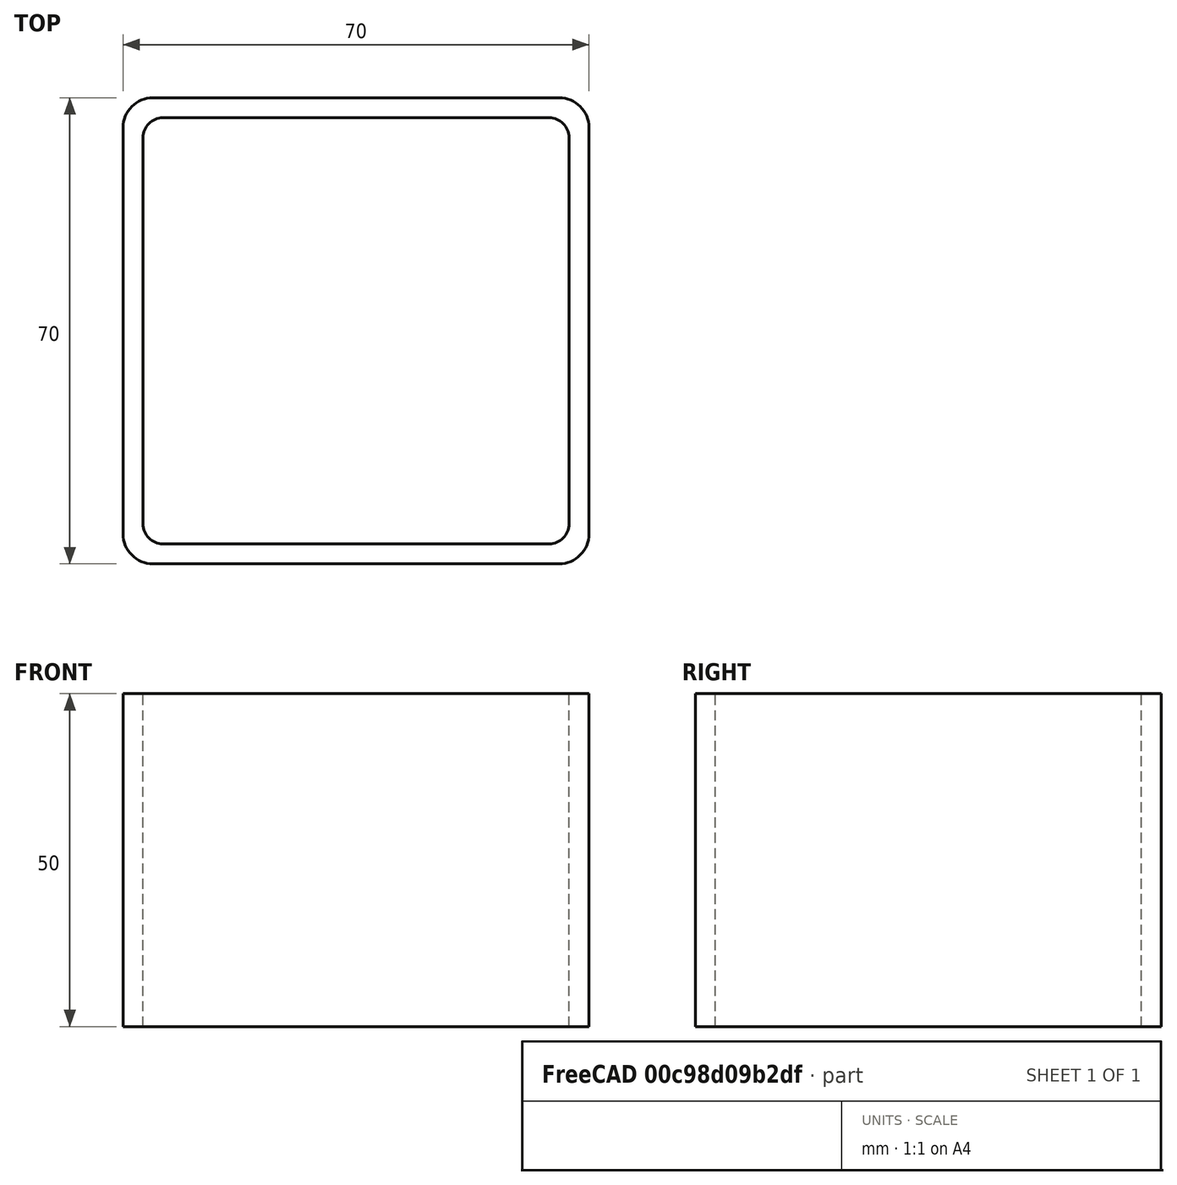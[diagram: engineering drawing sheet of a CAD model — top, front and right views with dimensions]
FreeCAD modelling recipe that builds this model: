
FCSTD DOCUMENT  (FreeCAD 0.15R4671 (Git))
Label: Square hollow section 70x70x3 EN10219 S235JRH
License: All rights reserved
LicenseURL: http://en.wikipedia.org/wiki/All_rights_reserved
objects: Sketcher::SketchObject×1, Part::Extrusion×1
note: 2 computed .brp shape members not serialized (recipe doc carries the construction recipe); baked Part::Feature solids carry a one-line shape summary decoded from their .brp

FEATURE [Sketcher::SketchObject] Sketch
  sketch-geometry (16):
    g0: LineSegment StartX=-29 StartY=32 StartZ=0 EndX=29 EndY=32 EndZ=0
    g1: LineSegment StartX=32 StartY=29 StartZ=0 EndX=32 EndY=-29 EndZ=0
    g2: LineSegment StartX=29 StartY=-32 StartZ=0 EndX=-29 EndY=-32 EndZ=0
    g3: LineSegment StartX=-32 StartY=-29 StartZ=0 EndX=-32 EndY=29 EndZ=0
    g4: LineSegment StartX=-30.5 StartY=35 StartZ=0 EndX=30.5 EndY=35 EndZ=0
    g5: LineSegment StartX=35 StartY=30.5 StartZ=0 EndX=35 EndY=-30.5 EndZ=0
    g6: LineSegment StartX=30.5 StartY=-35 StartZ=0 EndX=-30.5 EndY=-35 EndZ=0
    g7: LineSegment StartX=-35 StartY=-30.5 StartZ=0 EndX=-35 EndY=30.5 EndZ=0
    g8: ArcOfCircle CenterX=-29 CenterY=29 CenterZ=0 NormalX=0 NormalY=0 NormalZ=1 Radius=3 StartAngle=1.5708 EndAngle=3.14159
    g9: ArcOfCircle CenterX=29 CenterY=29 CenterZ=0 NormalX=0 NormalY=0 NormalZ=1 Radius=3 StartAngle=0 EndAngle=1.5708
    g10: ArcOfCircle CenterX=29 CenterY=-29 CenterZ=0 NormalX=0 NormalY=0 NormalZ=1 Radius=3 StartAngle=4.71239 EndAngle=6.28319
    g11: ArcOfCircle CenterX=-29 CenterY=-29 CenterZ=0 NormalX=0 NormalY=0 NormalZ=1 Radius=3 StartAngle=3.14159 EndAngle=4.71239
    g12: ArcOfCircle CenterX=30.5 CenterY=30.5 CenterZ=0 NormalX=0 NormalY=0 NormalZ=1 Radius=4.5 StartAngle=0 EndAngle=1.5708
    g13: ArcOfCircle CenterX=30.5 CenterY=-30.5 CenterZ=0 NormalX=0 NormalY=0 NormalZ=1 Radius=4.5 StartAngle=4.71239 EndAngle=6.28319
    g14: ArcOfCircle CenterX=-30.5 CenterY=-30.5 CenterZ=0 NormalX=0 NormalY=0 NormalZ=1 Radius=4.5 StartAngle=3.14159 EndAngle=4.71239
    g15: ArcOfCircle CenterX=-30.5 CenterY=30.5 CenterZ=0 NormalX=0 NormalY=0 NormalZ=1 Radius=4.5 StartAngle=1.5708 EndAngle=3.14159
  constraints (36):
    c: Horizontal(g2)
    c: Vertical(g3)
    c: Horizontal(g6)
    c: Vertical(g7)
    c: Tangent(g3,g8) = 1.5708
    c: Tangent(g0,g8) = 1.5708
    c: Tangent(g0,g9) = 1.5708
    c: Tangent(g1,g9) = 1.5708
    c: Tangent(g1,g10) = 1.5708
    c: Tangent(g2,g10) = 1.5708
    c: Tangent(g2,g11) = 1.5708
    c: Tangent(g3,g11) = 1.5708
    c: Tangent(g4,g12) = 1.5708
    c: Tangent(g5,g12) = 1.5708
    c: Tangent(g5,g13) = 1.5708
    c: Tangent(g6,g13) = 1.5708
    c: Tangent(g6,g14) = 1.5708
    c: Tangent(g7,g14) = 1.5708
    c: Tangent(g7,g15) = 1.5708
    c: Tangent(g4,g15) = 1.5708
    c: Equal(g9,g8)
    c: Equal(g9,g11)
    c: Equal(g9,g10)
    c: Equal(g12,g15)
    c: Equal(g12,g14)
    c: Equal(g12,g13)
    c: Symmetric(g4,g6,g-1)
    c: Symmetric(g7,g5,g-2)
    c: DistanceY(g4,g6) = -70
    c: DistanceX(g7,g5) = 70
    c: Symmetric(g3,g1,g-2)
    c: Symmetric(g0,g2,g-1)
    c: DistanceY(g0,g4) = 3
    c: DistanceX(g5,g1) = -3
    c: Radius(g9) = 3
    c: Radius(g12) = 4.5
FEATURE [Part::Extrusion] Extrude  label="Square hollow section 70x70x3 EN10219 S235JRH"
  Base = -> Sketch
  Dir = (0,0,50)
  Solid = true
